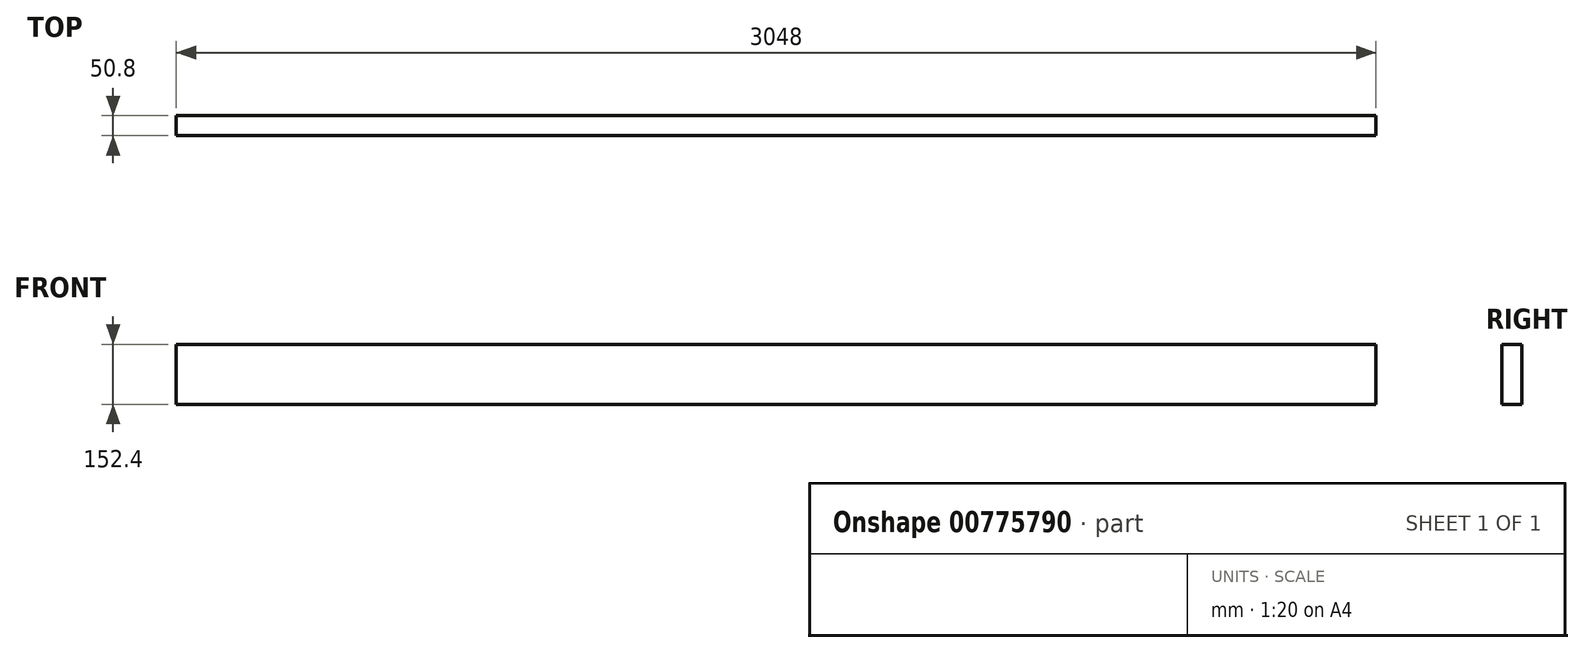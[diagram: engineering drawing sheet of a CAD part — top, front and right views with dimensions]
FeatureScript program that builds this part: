
annotation { "Feature Type Name" : "Feature", "Feature Type Description" : "" }
export const myFeature = defineFeature(function(context is Context, id is Id, definition is map)
    precondition{}
    {
        {
            var Q0;
            Q0=qCreatedBy(makeId("Top.planeOp"),FACE);
            var sketch = newSketch(context, id + "F0", { "sketchPlane" : qUnion([Q0])});
            skLineSegment(sketch, "E0.bottom", {"start": v(-1542.24, -690.43) * mm, "end": v(1505.76, -690.43) * mm});
            skLineSegment(sketch, "E0.top", {"start": v(-1542.24, -741.23) * mm, "end": v(1505.76, -741.23) * mm});
            skLineSegment(sketch, "E0.left", {"start": v(-1542.24, -690.43) * mm, "end": v(-1542.24, -741.23) * mm});
            skLineSegment(sketch, "E0.right", {"start": v(1505.76, -690.43) * mm, "end": v(1505.76, -741.23) * mm});
            skSolve(sketch);
        }
        {
            var Q0;
            Q0 = qSketchRegion(id + "F0", true);
            extrude(context, id + "F1", {"entities" : qUnion([Q0]), "depth" : 152.4 * mm, "offsetDistance" : 25.4 * mm});
        }
    });
